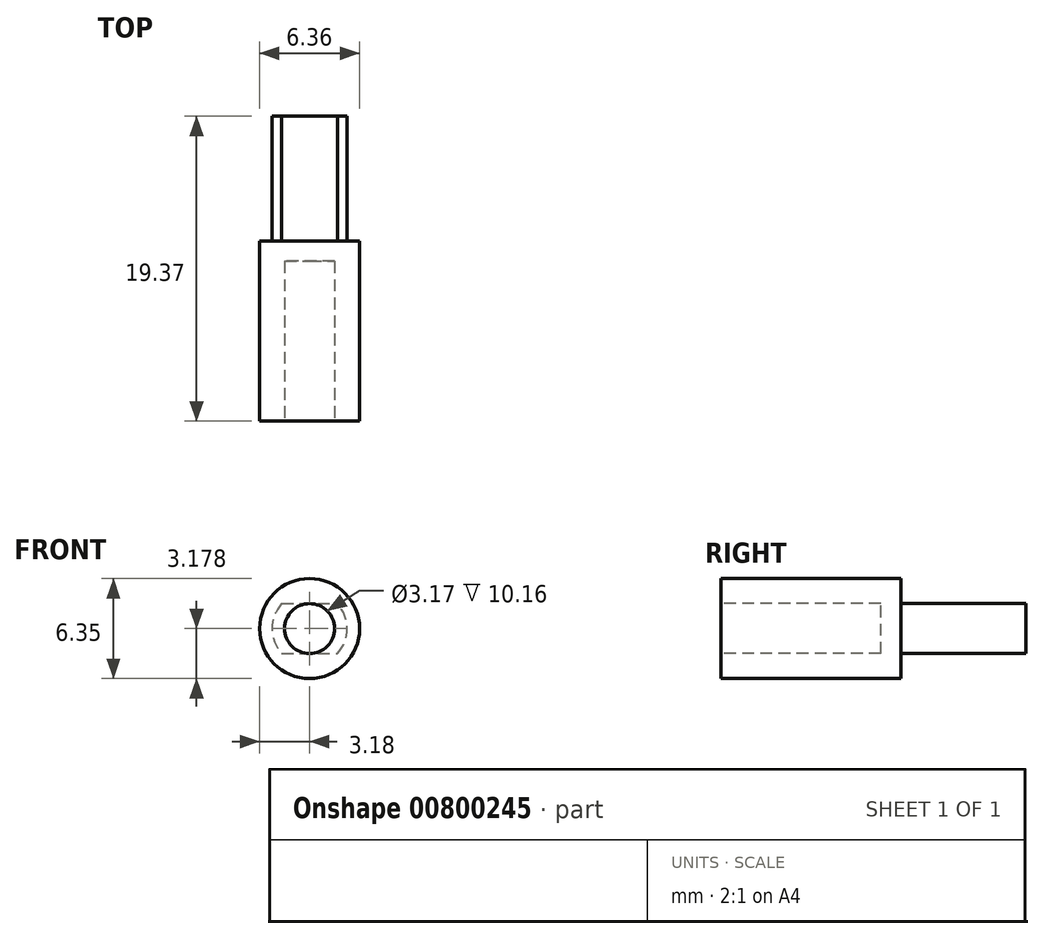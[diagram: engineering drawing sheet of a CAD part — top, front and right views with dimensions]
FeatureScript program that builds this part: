
annotation { "Feature Type Name" : "Feature", "Feature Type Description" : "" }
export const myFeature = defineFeature(function(context is Context, id is Id, definition is map)
    precondition{}
    {
        {
            var Q0;
            Q0=qCreatedBy(makeId("Front.planeOp"),FACE);
            var sketch = newSketch(context, id + "F0", { "sketchPlane" : qUnion([Q0])});
            skArc(sketch, "E0", {"start": v(1.77, 0) * mm, "mid": v(2.38, 1.59) * mm, "end": v(1.77, 3.17) * mm});
            skLineSegment(sketch, "E1", {"start": v(-1.77, 3.17) * mm, "end": v(1.77, 3.17) * mm});
            skLineSegment(sketch, "E2", {"start": v(-1.77, 0) * mm, "end": v(1.77, 0) * mm});
            skArc(sketch, "E3.trimOffspring", {"start": v(-1.77, 3.17) * mm, "mid": v(-2.38, 1.59) * mm, "end": v(-1.77, 0) * mm});
            skPoint(sketch, "E4.orphan", {"position": v(-4.94, 0) * mm});
            skSolve(sketch);
        }
        {
            var Q0;
            Q0=makeQuery(id+"F0.imprint","IMPRINT",FACE,{"disambiguationData":[TD([[makeQuery(id+"F0.imprint","IMPRINT",EDGE,{"derivedFrom":sQuery(id+"F0.wireOp",EDGE,"E0")}),1.0]])]});
            extrude(context, id + "F1", {"entities" : qUnion([Q0]), "oppositeDirection" : true, "depth" : 7.94 * mm, "offsetDistance" : 25.4 * mm});
        }
        {
            var Q0;
            Q0=makeQuery(id+"F1.opExtrude","CAP_FACE",FACE,{"disambiguationData":[OSD([sQuery(id+"F0.wireOp",EDGE,"E0"),sQuery(id+"F0.wireOp",EDGE,"E1"),sQuery(id+"F0.wireOp",EDGE,"E2"),sQuery(id+"F0.wireOp",EDGE,"E3.trimOffspring")])],"isStart":true});
            var sketch = newSketch(context, id + "F2", { "sketchPlane" : qUnion([Q0])});
            skCircle(sketch, "E5", {"center": v(0, 1.59) * mm, "radius": 3.18 * mm});
            skSolve(sketch);
        }
        {
            var Q0;
            Q0=makeQuery(id+"F2.imprint","IMPRINT",FACE,{"disambiguationData":[TD([[makeQuery(id+"F2.imprint","IMPRINT",EDGE,{"derivedFrom":makeQuery(id+"F1.opExtrude","CAP_EDGE",EDGE,{"disambiguationData":[OSD([sQuery(id+"F0.wireOp",EDGE,"E0")])],"isStart":true})}),1.0]])]});
            var Q1;
            Q1=makeQuery(id+"F2.imprint","IMPRINT",FACE,{"disambiguationData":[TD([[makeQuery(id+"F2.imprint","IMPRINT",EDGE,{"derivedFrom":sQuery(id+"F2.wireOp",EDGE,"E5")}),1.0]])]});
            extrude(context, id + "F3", {"entities" : qUnion([Q0, Q1]), "operationType" : NewBodyOperationType.ADD, "depth" : 11.43 * mm, "offsetDistance" : 25.4 * mm});
        }
        {
            var Q0;
            Q0=makeQuery(id+"F3.opExtrude","CAP_FACE",FACE,{"disambiguationData":[OSD([sQuery(id+"F2.wireOp",EDGE,"E5")])],"isStart":false});
            var sketch = newSketch(context, id + "F4", { "sketchPlane" : qUnion([Q0])});
            skCircle(sketch, "E6", {"center": v(0, 1.59) * mm, "radius": 1.59 * mm});
            skSolve(sketch);
        }
        {
            var Q0;
            Q0=makeQuery(id+"F4.imprint","IMPRINT",FACE,{"disambiguationData":[TD([[makeQuery(id+"F4.imprint","IMPRINT",EDGE,{"derivedFrom":sQuery(id+"F4.wireOp",EDGE,"E6")}),1.0]])]});
            extrude(context, id + "F5", {"entities" : qUnion([Q0]), "operationType" : NewBodyOperationType.REMOVE, "oppositeDirection" : true, "depth" : 10.16 * mm, "offsetDistance" : 25.4 * mm});
        }
    });
